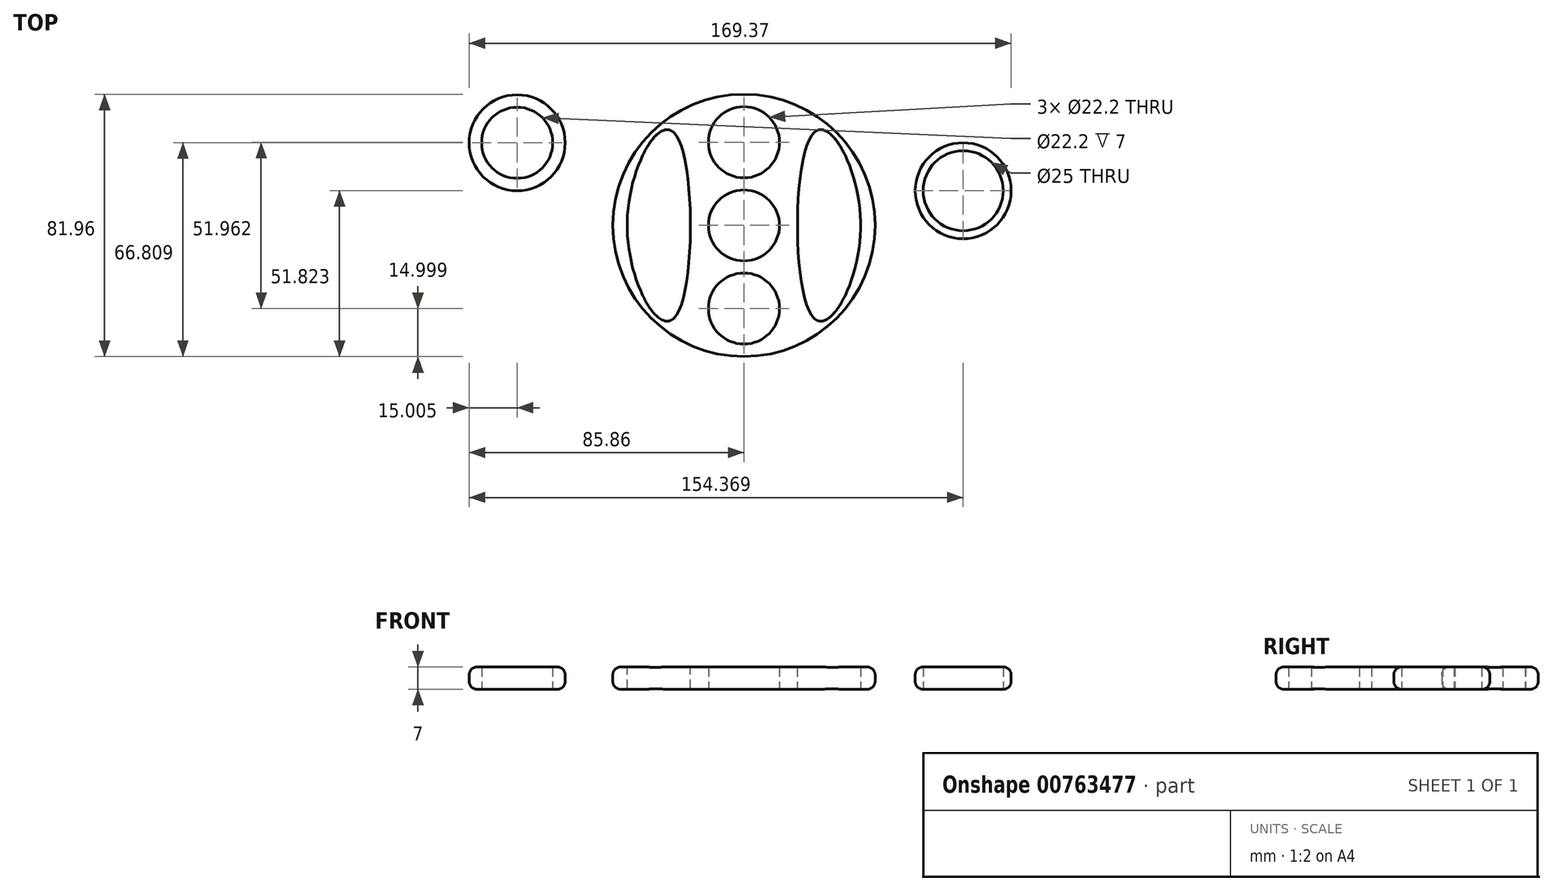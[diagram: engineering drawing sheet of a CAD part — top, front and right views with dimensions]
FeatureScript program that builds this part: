
annotation { "Feature Type Name" : "Feature", "Feature Type Description" : "" }
export const myFeature = defineFeature(function(context is Context, id is Id, definition is map)
    precondition{}
    {
        {
            var Q0;
            Q0=qCreatedBy(makeId("Top.planeOp"),FACE);
            var sketch = newSketch(context, id + "F0", { "sketchPlane" : qUnion([Q0])});
            skCircle(sketch, "E0", {"center": v(0, 0) * mm, "radius": 15 * mm});
            skPoint(sketch, "E1", {"position": v(15, 0) * mm});
            skArc(sketch, "E2", {"start": v(7.5, 13) * mm, "mid": v(0, 40.98) * mm, "end": v(-7.5, 13) * mm});
            skLineSegment(sketch, "E3", {"start": v(-63.54, 0) * mm, "end": v(62.86, 0) * mm, "construction": true});
            skArc(sketch, "E4.MirrorCS", {"start": v(7.5, -13) * mm, "mid": v(0, -40.98) * mm, "end": v(-7.5, -13) * mm});
            skCircle(sketch, "E5", {"center": v(0, 0) * mm, "radius": 11.1 * mm});
            skCircle(sketch, "E6", {"center": v(0, 25.98) * mm, "radius": 11.1 * mm});
            skCircle(sketch, "E7", {"center": v(0, -25.98) * mm, "radius": 11.1 * mm});
            skCircle(sketch, "E8", {"center": v(-70.86, 25.83) * mm, "radius": 15 * mm});
            skCircle(sketch, "E9", {"center": v(-70.86, 25.83) * mm, "radius": 11.1 * mm});
            skCircle(sketch, "E10", {"center": v(0, 0) * mm, "radius": 40.98 * mm});
            skCircle(sketch, "E11", {"center": v(68.5, 10.84) * mm, "radius": 15 * mm});
            skCircle(sketch, "E12", {"center": v(68.5, 10.84) * mm, "radius": 12.5 * mm});
            skLineSegment(sketch, "E13", {"start": v(0, 61.94) * mm, "end": v(0, -40.98) * mm, "construction": true});
            skPoint(sketch, "E13.startSnap0", {"position": v(0, 40.98) * mm});
            skLineSegment(sketch, "E14", {"start": v(-22, 29.1) * mm, "end": v(-22, -29.1) * mm});
            skFitSpline(sketch, "E15", {"points": [v(-22, 29.1) * mm, v(-36.49, 0) * mm, v(-22, -29.1) * mm, v(-22, 29.1) * mm]});
            skFitSpline(sketch, "E16.MirrorC", {"points": [v(22, 29.1) * mm, v(36.49, 0) * mm, v(22, -29.1) * mm, v(22, 29.1) * mm]});
            skLineSegment(sketch, "E17.MirrorCS", {"start": v(22, 29.1) * mm, "end": v(22, -29.1) * mm});
            skSolve(sketch);
        }
        {
            var Q0;
            Q0=qSketchRegion(id+"F0",true);
            var Q1;
            {var subQ2=sQuery(id+"F0.wireOp",EDGE,"E0");var subQ8=sQuery(id+"F0.wireOp",EDGE,"34ce2360-26bb-4ef9-a7d5-8eb1570df3c0");var subQ10=sQuery(id+"F0.wireOp",EDGE,"a9e61762-1184-48b9-b76d-7fac8632a7740.MirrorCS");var subQ11=makeQuery(id+"F0.imprint","INTERSECT",VERTEX,{"derivedFrom":[subQ2,subQ8,subQ10]});Q1=makeQuery(id+"F0.imprint","IMPRINT",FACE,{"disambiguationData":[TD([[makeQuery(id+"F0.imprint","IMPRINT",EDGE,{"disambiguationData":[TD([[subQ11,-1.0]])],"derivedFrom":subQ2}),1.0]])]});}
            var Q2;
            {var subQ1=sQuery(id+"F0.wireOp",EDGE,"1a58994c-98c9-4121-9ca7-f2efa985d20c");var subQ6=sQuery(id+"F0.wireOp",EDGE,"cZUj14hd-Wjng-dcA5-AEFl-M1aUuncTdPpW");var subQ7=makeQuery(id+"F0.imprint","INTERSECT",VERTEX,{"disambiguationData":[OD(1.0)],"derivedFrom":[subQ1,subQ6]});Q2=makeQuery(id+"F0.imprint","IMPRINT",FACE,{"disambiguationData":[TD([[makeQuery(id+"F0.imprint","IMPRINT",EDGE,{"disambiguationData":[TD([[subQ7,1.0]])],"derivedFrom":subQ6}),-1.0]])]});}
            var Q3;
            {var subQ0=sQuery(id+"F0.wireOp",EDGE,"E2");var subQ6=sQuery(id+"F0.wireOp",EDGE,"0jPJAtyu-uOoQ-rmUB-5DBI-f9QmJ9mnEyCU");var subQ8=makeQuery(id+"F0.imprint","INTERSECT",VERTEX,{"disambiguationData":[OD(1.0)],"derivedFrom":[subQ0,subQ6]});Q3=makeQuery(id+"F0.imprint","IMPRINT",FACE,{"disambiguationData":[TD([[makeQuery(id+"F0.imprint","IMPRINT",EDGE,{"disambiguationData":[TD([[subQ8,1.0]])],"derivedFrom":subQ6}),-1.0]])]});}
            var Q4;
            {var subQ1=sQuery(id+"F0.wireOp",EDGE,"34ce2360-26bb-4ef9-a7d5-8eb1570df3c0");var subQ6=sQuery(id+"F0.wireOp",EDGE,"E6");var subQ7=makeQuery(id+"F0.imprint","INTERSECT",VERTEX,{"disambiguationData":[OD(1.0)],"derivedFrom":[subQ1,subQ6]});Q4=makeQuery(id+"F0.imprint","IMPRINT",FACE,{"disambiguationData":[TD([[makeQuery(id+"F0.imprint","IMPRINT",EDGE,{"disambiguationData":[TD([[subQ7,1.0]])],"derivedFrom":subQ6}),-1.0]])]});}
            var Q5;
            {var subQ4=sQuery(id+"F0.wireOp",EDGE,"E2");var subQ6=sQuery(id+"F0.wireOp",EDGE,"Nfs40CQg-x6Bj-Incp-93SP-tW6It5nphqnA");var subQ7=makeQuery(id+"F0.imprint","INTERSECT",VERTEX,{"disambiguationData":[OD(0.0)],"derivedFrom":[subQ4,subQ6]});Q5=makeQuery(id+"F0.imprint","IMPRINT",FACE,{"disambiguationData":[TD([[makeQuery(id+"F0.imprint","IMPRINT",EDGE,{"disambiguationData":[TD([[subQ7,-1.0]])],"derivedFrom":subQ6}),-1.0]])]});}
            var Q6;
            {var subQ1=sQuery(id+"F0.wireOp",EDGE,"34ce2360-26bb-4ef9-a7d5-8eb1570df3c0");var subQ6=sQuery(id+"F0.wireOp",EDGE,"yfgWFcUV-c3Pj-H9RX-1UHe-zGKhwiYu3gs1");var subQ7=makeQuery(id+"F0.imprint","INTERSECT",VERTEX,{"disambiguationData":[OD(0.0)],"derivedFrom":[subQ1,subQ6]});Q6=makeQuery(id+"F0.imprint","IMPRINT",FACE,{"disambiguationData":[TD([[makeQuery(id+"F0.imprint","IMPRINT",EDGE,{"disambiguationData":[TD([[subQ7,-1.0]])],"derivedFrom":subQ6}),-1.0]])]});}
            var Q7;
            {var subQ1=sQuery(id+"F0.wireOp",EDGE,"a9e61762-1184-48b9-b76d-7fac8632a7740.MirrorCS");var subQ6=sQuery(id+"F0.wireOp",EDGE,"E7");var subQ7=makeQuery(id+"F0.imprint","INTERSECT",VERTEX,{"disambiguationData":[OD(1.0)],"derivedFrom":[subQ1,subQ6]});Q7=makeQuery(id+"F0.imprint","IMPRINT",FACE,{"disambiguationData":[TD([[makeQuery(id+"F0.imprint","IMPRINT",EDGE,{"disambiguationData":[TD([[subQ7,-1.0]])],"derivedFrom":subQ6}),-1.0]])]});}
            var Q8;
            {var subQ1=sQuery(id+"F0.wireOp",EDGE,"1a58994c-98c9-4121-9ca7-f2efa985d20c");var subQ5=sQuery(id+"F0.wireOp",EDGE,"E6");var subQ6=makeQuery(id+"F0.imprint","INTERSECT",VERTEX,{"disambiguationData":[OD(1.0)],"derivedFrom":[subQ1,subQ5]});Q8=makeQuery(id+"F0.imprint","IMPRINT",FACE,{"disambiguationData":[TD([[makeQuery(id+"F0.imprint","IMPRINT",EDGE,{"disambiguationData":[TD([[subQ6,-1.0]])],"derivedFrom":subQ1}),1.0]])]});}
            var Q9;
            {var subQ0=sQuery(id+"F0.wireOp",EDGE,"E2");var subQ1=sQuery(id+"F0.wireOp",EDGE,"1a58994c-98c9-4121-9ca7-f2efa985d20c");var subQ2=makeQuery(id+"F0.imprint","INTERSECT",VERTEX,{"derivedFrom":[subQ1,subQ0]});Q9=makeQuery(id+"F0.imprint","IMPRINT",FACE,{"disambiguationData":[TD([[makeQuery(id+"F0.imprint","IMPRINT",EDGE,{"disambiguationData":[TD([[subQ2,-1.0]])],"derivedFrom":subQ1}),1.0]])]});}
            var Q10;
            {var subQ0=sQuery(id+"F0.wireOp",EDGE,"4d966b77-e30a-4342-b6b6-06537614f87b0.MirrorCS");var subQ1=sQuery(id+"F0.wireOp",EDGE,"1a58994c-98c9-4121-9ca7-f2efa985d20c");var subQ2=makeQuery(id+"F0.imprint","INTERSECT",VERTEX,{"derivedFrom":[subQ1,subQ0]});Q10=makeQuery(id+"F0.imprint","IMPRINT",FACE,{"disambiguationData":[TD([[makeQuery(id+"F0.imprint","IMPRINT",EDGE,{"disambiguationData":[TD([[subQ2,-1.0]])],"derivedFrom":subQ1}),1.0]])]});}
            var Q11;
            {var subQ0=sQuery(id+"F0.wireOp",EDGE,"4d966b77-e30a-4342-b6b6-06537614f87b0.MirrorCS");var subQ1=sQuery(id+"F0.wireOp",EDGE,"1a58994c-98c9-4121-9ca7-f2efa985d20c");var subQ2=makeQuery(id+"F0.imprint","INTERSECT",VERTEX,{"derivedFrom":[subQ1,subQ0]});Q11=makeQuery(id+"F0.imprint","IMPRINT",FACE,{"disambiguationData":[TD([[makeQuery(id+"F0.imprint","IMPRINT",EDGE,{"disambiguationData":[TD([[subQ2,-1.0]])],"derivedFrom":subQ1}),-1.0]])]});}
            var Q12;
            {var subQ0=sQuery(id+"F0.wireOp",EDGE,"4d966b77-e30a-4342-b6b6-06537614f87b0.MirrorCS");var subQ1=sQuery(id+"F0.wireOp",EDGE,"E4.MirrorCS");var subQ7=makeQuery(id+"F0.imprint","INTERSECT",VERTEX,{"derivedFrom":[subQ1,subQ0]});Q12=makeQuery(id+"F0.imprint","IMPRINT",FACE,{"disambiguationData":[TD([[makeQuery(id+"F0.imprint","IMPRINT",EDGE,{"disambiguationData":[TD([[subQ7,-1.0]])],"derivedFrom":subQ1}),-1.0]])]});}
            var Q13;
            {var subQ0=sQuery(id+"F0.wireOp",EDGE,"E4.MirrorCS");var subQ1=sQuery(id+"F0.wireOp",EDGE,"a9e61762-1184-48b9-b76d-7fac8632a7740.MirrorCS");var subQ2=makeQuery(id+"F0.imprint","INTERSECT",VERTEX,{"derivedFrom":[subQ1,subQ0]});Q13=makeQuery(id+"F0.imprint","IMPRINT",FACE,{"disambiguationData":[TD([[makeQuery(id+"F0.imprint","IMPRINT",EDGE,{"disambiguationData":[TD([[subQ2,-1.0]])],"derivedFrom":subQ1}),1.0]])]});}
            var Q14;
            {var subQ0=sQuery(id+"F0.wireOp",EDGE,"E4.MirrorCS");var subQ1=sQuery(id+"F0.wireOp",EDGE,"a9e61762-1184-48b9-b76d-7fac8632a7740.MirrorCS");var subQ7=makeQuery(id+"F0.imprint","INTERSECT",VERTEX,{"derivedFrom":[subQ1,subQ0]});Q14=makeQuery(id+"F0.imprint","IMPRINT",FACE,{"disambiguationData":[TD([[makeQuery(id+"F0.imprint","IMPRINT",EDGE,{"disambiguationData":[TD([[subQ7,-1.0]])],"derivedFrom":subQ1}),-1.0]])]});}
            var Q15;
            {var subQ0=sQuery(id+"F0.wireOp",EDGE,"yfgWFcUV-c3Pj-H9RX-1UHe-zGKhwiYu3gs1");var subQ1=sQuery(id+"F0.wireOp",EDGE,"34ce2360-26bb-4ef9-a7d5-8eb1570df3c0");var subQ2=makeQuery(id+"F0.imprint","INTERSECT",VERTEX,{"disambiguationData":[OD(1.0)],"derivedFrom":[subQ1,subQ0]});Q15=makeQuery(id+"F0.imprint","IMPRINT",FACE,{"disambiguationData":[TD([[makeQuery(id+"F0.imprint","IMPRINT",EDGE,{"disambiguationData":[TD([[subQ2,-1.0]])],"derivedFrom":subQ1}),-1.0]])]});}
            var Q16;
            {var subQ1=sQuery(id+"F0.wireOp",EDGE,"34ce2360-26bb-4ef9-a7d5-8eb1570df3c0");var subQ7=sQuery(id+"F0.wireOp",EDGE,"yfgWFcUV-c3Pj-H9RX-1UHe-zGKhwiYu3gs1");var subQ8=makeQuery(id+"F0.imprint","INTERSECT",VERTEX,{"disambiguationData":[OD(1.0)],"derivedFrom":[subQ1,subQ7]});Q16=makeQuery(id+"F0.imprint","IMPRINT",FACE,{"disambiguationData":[TD([[makeQuery(id+"F0.imprint","IMPRINT",EDGE,{"disambiguationData":[TD([[subQ8,-1.0]])],"derivedFrom":subQ1}),1.0]])]});}
            var Q17;
            {var subQ0=sQuery(id+"F0.wireOp",EDGE,"a9e61762-1184-48b9-b76d-7fac8632a7740.MirrorCS");var subQ1=sQuery(id+"F0.wireOp",EDGE,"34ce2360-26bb-4ef9-a7d5-8eb1570df3c0");var subQ2=makeQuery(id+"F0.imprint","INTERSECT",VERTEX,{"derivedFrom":[subQ1,subQ0]});Q17=makeQuery(id+"F0.imprint","IMPRINT",FACE,{"disambiguationData":[TD([[makeQuery(id+"F0.imprint","IMPRINT",EDGE,{"disambiguationData":[TD([[subQ2,-1.0]])],"derivedFrom":subQ1}),1.0]])]});}
            var Q18;
            {var subQ0=sQuery(id+"F0.wireOp",EDGE,"E2");var subQ1=sQuery(id+"F0.wireOp",EDGE,"34ce2360-26bb-4ef9-a7d5-8eb1570df3c0");var subQ2=makeQuery(id+"F0.imprint","INTERSECT",VERTEX,{"derivedFrom":[subQ1,subQ0]});Q18=makeQuery(id+"F0.imprint","IMPRINT",FACE,{"disambiguationData":[TD([[makeQuery(id+"F0.imprint","IMPRINT",EDGE,{"disambiguationData":[TD([[subQ2,-1.0]])],"derivedFrom":subQ1}),1.0]])]});}
            var Q19;
            {var subQ0=sQuery(id+"F0.wireOp",EDGE,"E2");var subQ1=sQuery(id+"F0.wireOp",EDGE,"34ce2360-26bb-4ef9-a7d5-8eb1570df3c0");var subQ2=makeQuery(id+"F0.imprint","INTERSECT",VERTEX,{"derivedFrom":[subQ1,subQ0]});Q19=makeQuery(id+"F0.imprint","IMPRINT",FACE,{"disambiguationData":[TD([[makeQuery(id+"F0.imprint","IMPRINT",EDGE,{"disambiguationData":[TD([[subQ2,-1.0]])],"derivedFrom":subQ1}),-1.0]])]});}
            var Q20;
            {var subQ0=sQuery(id+"F0.wireOp",EDGE,"a9e61762-1184-48b9-b76d-7fac8632a7740.MirrorCS");var subQ1=sQuery(id+"F0.wireOp",EDGE,"34ce2360-26bb-4ef9-a7d5-8eb1570df3c0");var subQ3=makeQuery(id+"F0.imprint","INTERSECT",VERTEX,{"derivedFrom":[subQ1,subQ0]});Q20=makeQuery(id+"F0.imprint","IMPRINT",FACE,{"disambiguationData":[TD([[makeQuery(id+"F0.imprint","IMPRINT",EDGE,{"disambiguationData":[TD([[subQ3,1.0]])],"derivedFrom":subQ1}),1.0]])]});}
            var Q21;
            {var subQ0=sQuery(id+"F0.wireOp",EDGE,"E2");var subQ1=sQuery(id+"F0.wireOp",EDGE,"1a58994c-98c9-4121-9ca7-f2efa985d20c");var subQ3=makeQuery(id+"F0.imprint","INTERSECT",VERTEX,{"derivedFrom":[subQ1,subQ0]});Q21=makeQuery(id+"F0.imprint","IMPRINT",FACE,{"disambiguationData":[TD([[makeQuery(id+"F0.imprint","IMPRINT",EDGE,{"disambiguationData":[TD([[subQ3,1.0]])],"derivedFrom":subQ1}),1.0]])]});}
            extrude(context, id + "F1", {"entities" : qUnion([Q0, Q1, Q2, Q3, Q4, Q5, Q6, Q7, Q8, Q9, Q10, Q11, Q12, Q13, Q14, Q15, Q16, Q17, Q18, Q19, Q20, Q21]), "depth" : 7 * mm, "offsetDistance" : 25.4 * mm});
        }
        {
            var Q0;
            Q0=makeQuery(id+"F1.opExtrude","CAP_EDGE",EDGE,{"disambiguationData":[OSD([sQuery(id+"F0.wireOp",EDGE,"E10")])],"isStart":false});
            var Q1;
            Q1=makeQuery(id+"F1.opExtrude","CAP_EDGE",EDGE,{"disambiguationData":[OSD([sQuery(id+"F0.wireOp",EDGE,"E10")])],"isStart":true});
            var Q2;
            Q2=makeQuery(id+"F1.opExtrude","CAP_EDGE",EDGE,{"disambiguationData":[OSD([sQuery(id+"F0.wireOp",EDGE,"E11")])],"isStart":false});
            var Q3;
            Q3=makeQuery(id+"F1.opExtrude","CAP_EDGE",EDGE,{"disambiguationData":[OSD([sQuery(id+"F0.wireOp",EDGE,"E11")])],"isStart":true});
            var Q4;
            Q4=makeQuery(id+"F1.opExtrude","CAP_EDGE",EDGE,{"disambiguationData":[OSD([sQuery(id+"F0.wireOp",EDGE,"E8")])],"isStart":true});
            var Q5;
            Q5=makeQuery(id+"F1.opExtrude","CAP_EDGE",EDGE,{"disambiguationData":[OSD([sQuery(id+"F0.wireOp",EDGE,"E8")])],"isStart":false});
            fillet(context, id + "F2", {"entities" : qUnion([Q0, Q1, Q2, Q3, Q4, Q5]), "radius" : 2.5 * mm, "tangentPropagation" : true, "allowEdgeOverflow" : false});
        }
    });
